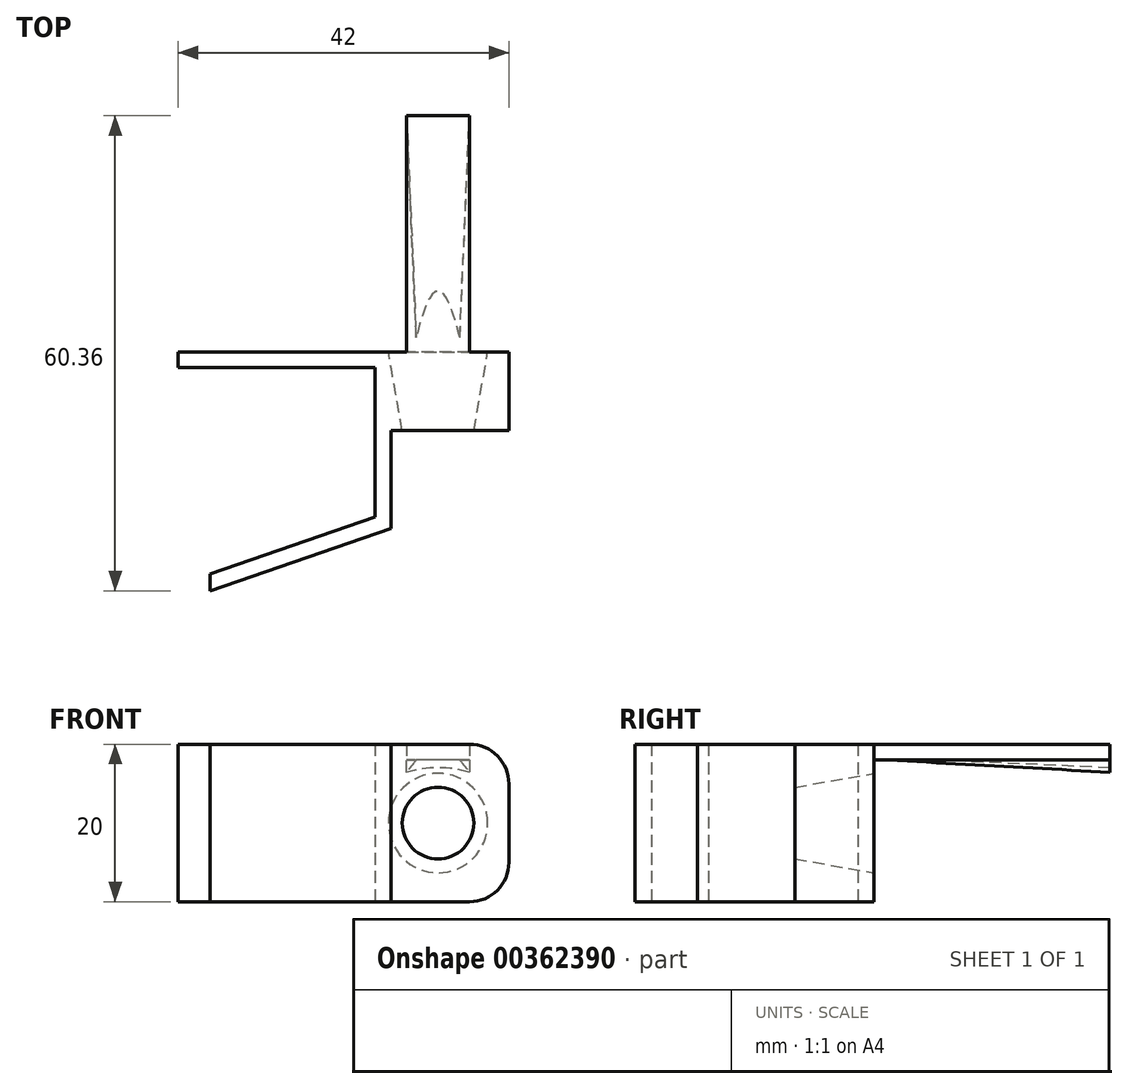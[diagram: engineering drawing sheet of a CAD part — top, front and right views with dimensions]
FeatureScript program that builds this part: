
annotation { "Feature Type Name" : "Feature", "Feature Type Description" : "" }
export const myFeature = defineFeature(function(context is Context, id is Id, definition is map)
    precondition{}
    {
        {
            var Q0;
            Q0=qCreatedBy(makeId("Top.planeOp"),FACE);
            var sketch = newSketch(context, id + "F0", { "sketchPlane" : qUnion([Q0])});
            skLineSegment(sketch, "E0", {"start": v(-61.58, 2.99) * mm, "end": v(-36.58, 2.99) * mm});
            skLineSegment(sketch, "E1", {"start": v(-36.58, 2.99) * mm, "end": v(-36.58, -16.01) * mm});
            skLineSegment(sketch, "E2", {"start": v(-36.58, -16.01) * mm, "end": v(-57.5, -23.25) * mm});
            skLineSegment(sketch, "E3", {"start": v(-57.5, -23.25) * mm, "end": v(-57.5, -25.37) * mm});
            skLineSegment(sketch, "E4", {"start": v(-57.5, -25.37) * mm, "end": v(-34.58, -17.44) * mm});
            skLineSegment(sketch, "E5", {"start": v(-19.58, 4.99) * mm, "end": v(-61.58, 4.99) * mm});
            skLineSegment(sketch, "E6", {"start": v(-61.58, 4.99) * mm, "end": v(-61.58, 2.99) * mm});
            skLineSegment(sketch, "E7", {"start": v(-34.58, -17.44) * mm, "end": v(-34.58, -5.01) * mm});
            skLineSegment(sketch, "E8", {"start": v(-34.58, -5.01) * mm, "end": v(-19.58, -5.01) * mm});
            skLineSegment(sketch, "E9", {"start": v(-19.58, -5.01) * mm, "end": v(-19.58, 4.99) * mm});
            skSolve(sketch);
        }
        {
            var Q0;
            Q0 = qSketchRegion(id + "F0", true);
            extrude(context, id + "F1", {"entities" : qUnion([Q0]), "depth" : 20 * mm});
        }
        {
            var Q0;
            Q0=makeQuery(id+"F1.opExtrude","SWEPT_FACE",FACE,{"disambiguationData":[OSD([sQuery(id+"F0.wireOp",EDGE,"E5")])]});
            var sketch = newSketch(context, id + "F2", { "sketchPlane" : qUnion([Q0])});
            skCircle(sketch, "E10", {"center": v(28.58, 10) * mm, "radius": 6.32 * mm});
            skSolve(sketch);
        }
        {
            var Q0;
            Q0 = qSketchRegion(id + "F2", true);
            extrude(context, id + "F3", {"entities" : qUnion([Q0]), "operationType" : NewBodyOperationType.REMOVE, "oppositeDirection" : true, "depth" : 10 * mm, "hasDraft" : true, "draftAngle" : 10 * degree, "draftPullDirection" : true});
        }
        {
            var Q0;
            Q0=makeQuery(id+"F1.opExtrude","CAP_EDGE",EDGE,{"disambiguationData":[OSD([sQuery(id+"F0.wireOp",EDGE,"E9")])],"isStart":false});
            var Q1;
            Q1=makeQuery(id+"F1.opExtrude","CAP_EDGE",EDGE,{"disambiguationData":[OSD([sQuery(id+"F0.wireOp",EDGE,"E9")])],"isStart":true});
            fillet(context, id + "F4", {"entities" : qUnion([Q0, Q1]), "radius" : 5 * mm, "tangentPropagation" : true, "allowEdgeOverflow" : false});
        }
        {
            var Q0;
            Q0=makeQuery(id+"F1.opExtrude","SWEPT_FACE",FACE,{"disambiguationData":[OSD([sQuery(id+"F0.wireOp",EDGE,"E5")])]});
            var sketch = newSketch(context, id + "F5", { "sketchPlane" : qUnion([Q0])});
            skLineSegment(sketch, "E11.bottom", {"start": v(24.58, 20) * mm, "end": v(32.58, 20) * mm});
            skLineSegment(sketch, "E11.top", {"start": v(24.58, 18) * mm, "end": v(32.58, 18) * mm});
            skLineSegment(sketch, "E11.left", {"start": v(24.58, 20) * mm, "end": v(24.58, 18) * mm});
            skLineSegment(sketch, "E11.right", {"start": v(32.58, 20) * mm, "end": v(32.58, 18) * mm});
            skSolve(sketch);
        }
        {
            var Q0;
            Q0 = qSketchRegion(id + "F5", true);
            extrude(context, id + "F6", {"entities" : qUnion([Q0]), "operationType" : NewBodyOperationType.ADD, "depth" : 30 * mm});
        }
        {
            var Q0;
            Q0=makeQuery(id+"F6.opExtrude","CAP_FACE",FACE,{"disambiguationData":[OSD([sQuery(id+"F5.wireOp",EDGE,"E11.bottom"),sQuery(id+"F5.wireOp",EDGE,"E11.top"),sQuery(id+"F5.wireOp",EDGE,"E11.left"),sQuery(id+"F5.wireOp",EDGE,"E11.right")])],"isStart":false});
            var sketch = newSketch(context, id + "F7", { "sketchPlane" : qUnion([Q0])});
            skLineSegment(sketch, "E12", {"start": v(24.58, 16.43) * mm, "end": v(24.58, 20) * mm});
            skLineSegment(sketch, "E13", {"start": v(24.58, 20) * mm, "end": v(32.58, 20) * mm});
            skLineSegment(sketch, "E14", {"start": v(32.58, 20) * mm, "end": v(32.58, 16.43) * mm});
            skPoint(sketch, "E15.endSnap0", {"position": v(24.58, 18.22) * mm});
            skArc(sketch, "E16", {"start": v(32.58, 16.43) * mm, "mid": v(28.58, 17.03) * mm, "end": v(24.58, 16.43) * mm});
            skSolve(sketch);
        }
        {
            var Q0;
            Q0 = qSketchRegion(id + "F7", true);
            extrude(context, id + "F8", {"entities" : qUnion([Q0]), "operationType" : NewBodyOperationType.ADD, "oppositeDirection" : true, "depth" : 30 * mm, "hasDraft" : true, "draftAngle" : 2.5 * degree, "draftPullDirection" : true});
        }
    });
